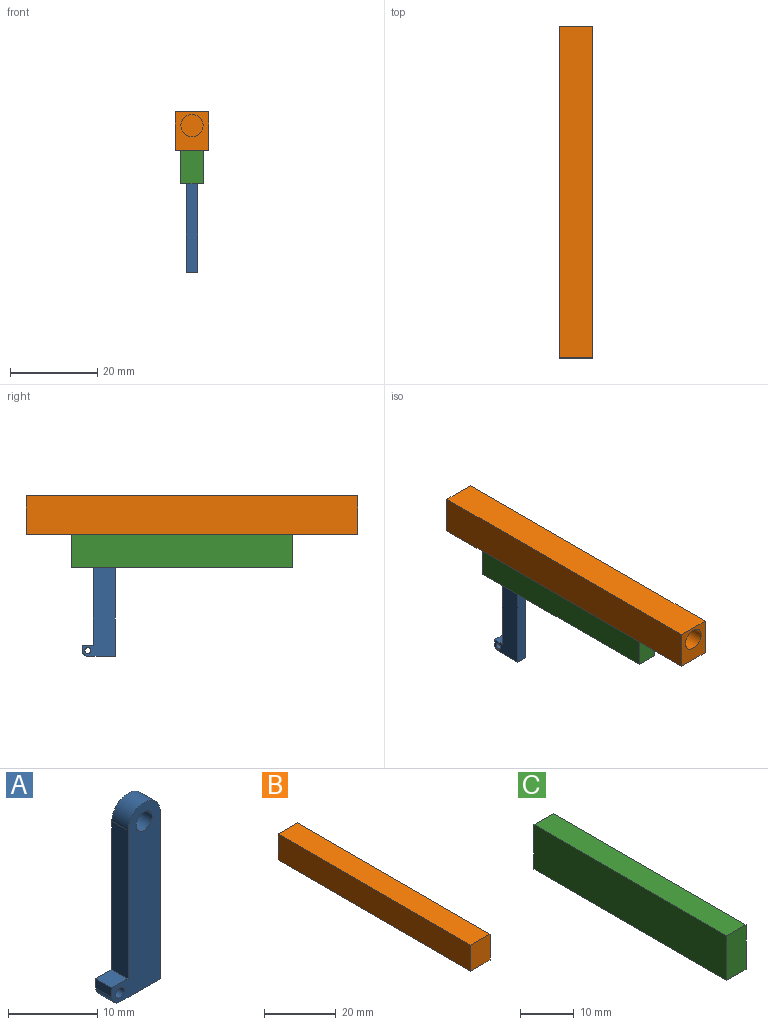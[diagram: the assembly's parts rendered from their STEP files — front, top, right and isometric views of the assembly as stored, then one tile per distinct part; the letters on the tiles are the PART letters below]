
ASSEMBLY  parts=3 mates=2
PART A: 11 faces, bbox 7.6x2.5x25.4 mm
  f0: plane 6.35x2.54mm, normal (0,0,-1), area 16.1mm2, adj f2,f3,f7,f9
  f1: plane 2.54x1.27mm, normal (-1,0,0), area 3.2mm2, adj f2,f3,f9,f10
  f2: plane 25.39x7.62mm, normal (0,-1,0), area 125.8mm2, adj f0,f1,f4,f5,f6,f7,f8,f9
  f3: plane 25.39x7.62mm, normal (0,1,0), area 125.8mm2, adj f0,f1,f4,f5,f6,f7,f8,f9
  f4: cylinder r=2.54mm len=5.08mm, axis (0,1,0), area 20.2mm2, adj f2,f3,f5,f7
  f5: plane 20.32x2.54mm, normal (-1,0,0), area 51.6mm2, adj f2,f3,f4,f10
  f6: cylinder r=1.27mm len=2.54mm, axis (0,1,0), area 20.3mm2, adj f2,f3
  f7: plane 22.86x2.54mm, normal (1,0,0), area 58.1mm2, adj f0,f2,f3,f4
  f8: cylinder r=0.68mm len=2.54mm, axis (0,-1,0), area 10.9mm2, adj f2,f3
  f9: cylinder r=1.27mm len=2.54mm, axis (0,-1,0), area 5.1mm2, adj f0,f1,f2,f3
  f10: plane 2.54x2.54mm, normal (0,0,1), area 6.5mm2, adj f1,f2,f3,f5
PART B: 13 faces, bbox 7.6x76.2x8.9 mm
  f0: plane 76.2x8.89mm, normal (-1,0,0), area 677.4mm2, adj f1,f3,f4,f9
  f1: plane 8.89x7.62mm, normal (0,-1,0), area 67.7mm2, adj f0,f2,f4,f9
  f2: plane 76.2x8.89mm, normal (1,0,0), area 677.4mm2, adj f1,f3,f4,f9
  f3: plane 8.89x7.62mm, normal (0,1,0), area 47.5mm2, adj f0,f2,f4,f9,f11
  f4: plane 76.2x7.62mm, normal (0,0,1), area 580.6mm2, adj f0,f1,f2,f3
  f5: plane 5.08x2.54mm, normal (0,1,0), area 12.9mm2, adj f6,f8,f9,f10
  f6: plane 50.8x2.54mm, normal (1,0,0), area 129mm2, adj f5,f7,f9,f10
  f7: plane 5.08x2.54mm, normal (0,-1,0), area 12.9mm2, adj f6,f8,f9,f10
  f8: plane 50.8x2.54mm, normal (-1,0,0), area 129mm2, adj f5,f7,f9,f10
  f9: plane 76.2x7.62mm, normal (0,0,-1), area 322.6mm2, adj f0,f1,f2,f3,f5,f6,f7,f8
  f10: plane 50.8x5.08mm, normal (0,0,-1), area 258.1mm2, adj f5,f6,f7,f8
  f11: cylinder r=2.54mm len=25.4mm, axis (0,1,0), area 405.4mm2, adj f3,f12
  f12: plane 5.08x5.08mm, normal (0,1,0), area 20.3mm2, adj f11
PART C: 12 faces, bbox 5.1x50.8x10.2 mm
  f0: plane 10.16x5.08mm, normal (0,1,0), area 51.6mm2, adj f1,f3,f4,f5
  f1: plane 50.8x10.16mm, normal (-1,0,0), area 516.1mm2, adj f0,f2,f4,f5
  f2: plane 10.16x5.08mm, normal (0,-1,0), area 51.6mm2, adj f1,f3,f4,f5
  f3: plane 50.8x10.16mm, normal (1,0,0), area 516.1mm2, adj f0,f2,f4,f5
  f4: plane 50.8x5.08mm, normal (0,0,1), area 258.1mm2, adj f0,f1,f2,f3
  f5: plane 50.8x5.08mm, normal (0,0,-1), area 161.3mm2, adj f0,f1,f2,f3,f6,f7,f8,f9
  f6: plane 5.08x2.54mm, normal (0,1,0), area 12.9mm2, adj f5,f7,f9,f10
  f7: plane 38.1x5.08mm, normal (-1,0,0), area 188.5mm2, adj f5,f6,f8,f10,f11
  f8: plane 5.08x2.54mm, normal (0,-1,0), area 12.9mm2, adj f5,f7,f9,f10
  f9: plane 38.1x5.08mm, normal (1,0,0), area 188.5mm2, adj f5,f6,f8,f10,f11
  f10: plane 38.1x2.54mm, normal (0,0,-1), area 96.8mm2, adj f6,f7,f8,f9
  f11: cylinder r=1.27mm len=2.54mm, axis (1,0,0), area 20.3mm2, adj f7,f9
PLACE A rot(axis=(0,0,-1),90deg) t=(-1.38,-15.15,-6.53)mm
PLACE B rot(axis=(0,0,1),180deg) t=(-13.88,4.03,3.02)mm
PLACE C t=(8.91,2.14,-7.14)mm
MATE cylindrical A.f6 <-> C.f11  axis (1,0,0) through (-3.92,20.19,-4.6)mm
MATE planar B.f10 <-> C.f4  axis (0,0,-1) through (-2.65,0.08,3.02)mm
